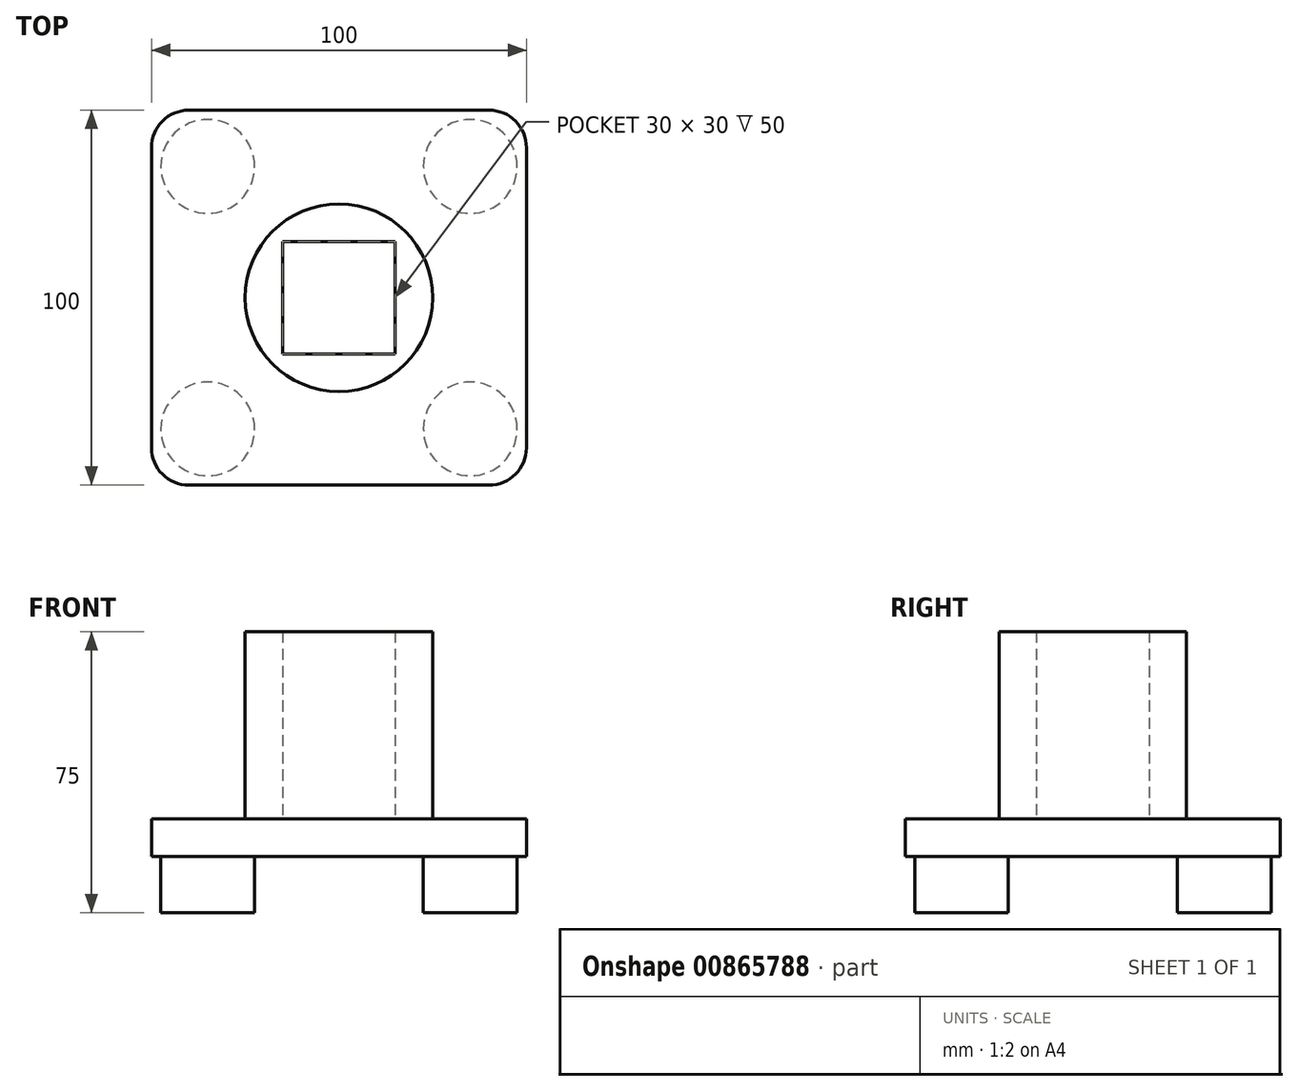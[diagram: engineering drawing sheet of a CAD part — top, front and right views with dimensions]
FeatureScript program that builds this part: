
annotation { "Feature Type Name" : "Feature", "Feature Type Description" : "" }
export const myFeature = defineFeature(function(context is Context, id is Id, definition is map)
    precondition{}
    {
        {
            var Q0;
            Q0=qCreatedBy(makeId("Front.planeOp"),FACE);
            var sketch = newSketch(context, id + "F0", { "sketchPlane" : qUnion([Q0])});
            skLineSegment(sketch, "E0.bottom", {"start": v(50, 5) * mm, "end": v(-50, 5) * mm});
            skLineSegment(sketch, "E0.top", {"start": v(50, -5) * mm, "end": v(-50, -5) * mm});
            skLineSegment(sketch, "E0.left", {"start": v(50, 5) * mm, "end": v(50, -5) * mm});
            skLineSegment(sketch, "E0.right", {"start": v(-50, 5) * mm, "end": v(-50, -5) * mm});
            skPoint(sketch, "E0.middle", {"position": v(0, 0) * mm});
            skSolve(sketch);
        }
        {
            var Q0;
            Q0=makeQuery(id+"F0.imprint","IMPRINT",FACE,{"disambiguationData":[TD([[makeQuery(id+"F0.imprint","IMPRINT",EDGE,{"derivedFrom":sQuery(id+"F0.wireOp",EDGE,"E0.bottom")}),1.0]])]});
            extrude(context, id + "F1", {"entities" : qUnion([Q0]), "endBound" : BoundingType.SYMMETRIC, "depth" : 100 * mm});
        }
        {
            var Q0;
            Q0=makeQuery(id+"F1.opExtrude","SWEPT_FACE",FACE,{"disambiguationData":[OSD([sQuery(id+"F0.wireOp",EDGE,"E0.top")])]});
            var sketch = newSketch(context, id + "F2", { "sketchPlane" : qUnion([Q0])});
            skCircle(sketch, "E1", {"center": v(-35, 35) * mm, "radius": 12.5 * mm});
            skCircle(sketch, "E2", {"center": v(35, 35) * mm, "radius": 12.5 * mm});
            skCircle(sketch, "E3", {"center": v(-35, -35) * mm, "radius": 12.5 * mm});
            skCircle(sketch, "E4", {"center": v(35, -35) * mm, "radius": 12.5 * mm});
            skSolve(sketch);
        }
        {
            var Q0;
            Q0=makeQuery(id+"F2.imprint","IMPRINT",FACE,{"disambiguationData":[TD([[makeQuery(id+"F2.imprint","IMPRINT",EDGE,{"derivedFrom":sQuery(id+"F2.wireOp",EDGE,"E2")}),1.0]])]});
            var Q1;
            Q1=makeQuery(id+"F2.imprint","IMPRINT",FACE,{"disambiguationData":[TD([[makeQuery(id+"F2.imprint","IMPRINT",EDGE,{"derivedFrom":sQuery(id+"F2.wireOp",EDGE,"E4")}),1.0]])]});
            var Q2;
            Q2=makeQuery(id+"F2.imprint","IMPRINT",FACE,{"disambiguationData":[TD([[makeQuery(id+"F2.imprint","IMPRINT",EDGE,{"derivedFrom":sQuery(id+"F2.wireOp",EDGE,"E3")}),1.0]])]});
            var Q3;
            Q3=makeQuery(id+"F2.imprint","IMPRINT",FACE,{"disambiguationData":[TD([[makeQuery(id+"F2.imprint","IMPRINT",EDGE,{"derivedFrom":sQuery(id+"F2.wireOp",EDGE,"E1")}),1.0]])]});
            extrude(context, id + "F3", {"entities" : qUnion([Q0, Q1, Q2, Q3]), "operationType" : NewBodyOperationType.ADD, "depth" : 15 * mm});
        }
        {
            var Q0;
            Q0=makeQuery(id+"F1.opExtrude","CAP_EDGE",EDGE,{"disambiguationData":[OSD([sQuery(id+"F0.wireOp",EDGE,"E0.right")])],"isStart":false});
            var Q1;
            Q1=makeQuery(id+"F1.opExtrude","CAP_EDGE",EDGE,{"disambiguationData":[OSD([sQuery(id+"F0.wireOp",EDGE,"E0.left")])],"isStart":false});
            var Q2;
            Q2=makeQuery(id+"F1.opExtrude","CAP_EDGE",EDGE,{"disambiguationData":[OSD([sQuery(id+"F0.wireOp",EDGE,"E0.left")])],"isStart":true});
            var Q3;
            Q3=makeQuery(id+"F1.opExtrude","CAP_EDGE",EDGE,{"disambiguationData":[OSD([sQuery(id+"F0.wireOp",EDGE,"E0.right")])],"isStart":true});
            fillet(context, id + "F4", {"entities" : qUnion([Q0, Q1, Q2, Q3]), "radius" : 10 * mm, "tangentPropagation" : true, "allowEdgeOverflow" : false});
        }
        {
            var Q0;
            Q0=makeQuery(id+"F1.opExtrude","SWEPT_FACE",FACE,{"disambiguationData":[OSD([sQuery(id+"F0.wireOp",EDGE,"E0.bottom")])]});
            var sketch = newSketch(context, id + "F5", { "sketchPlane" : qUnion([Q0])});
            skCircle(sketch, "E5", {"center": v(0, 0) * mm, "radius": 25 * mm});
            skLineSegment(sketch, "E6.left", {"start": v(1.59, 0) * mm, "end": v(1.59, 0) * mm});
            skPoint(sketch, "E6.middle", {"position": v(1.59, 0) * mm});
            skLineSegment(sketch, "E7.bottom", {"start": v(15, 15) * mm, "end": v(-15, 15) * mm});
            skLineSegment(sketch, "E7.top", {"start": v(15, -15) * mm, "end": v(-15, -15) * mm});
            skLineSegment(sketch, "E7.left", {"start": v(15, 15) * mm, "end": v(15, -15) * mm});
            skLineSegment(sketch, "E7.right", {"start": v(-15, 15) * mm, "end": v(-15, -15) * mm});
            skSolve(sketch);
        }
        {
            var Q0;
            Q0=makeQuery(id+"F5.imprint","IMPRINT",FACE,{"disambiguationData":[TD([[makeQuery(id+"F5.imprint","IMPRINT",EDGE,{"derivedFrom":sQuery(id+"F5.wireOp",EDGE,"E5")}),1.0]])]});
            extrude(context, id + "F6", {"entities" : qUnion([Q0]), "operationType" : NewBodyOperationType.ADD, "depth" : 50 * mm, "offsetDistance" : 25 * mm});
        }
    });
